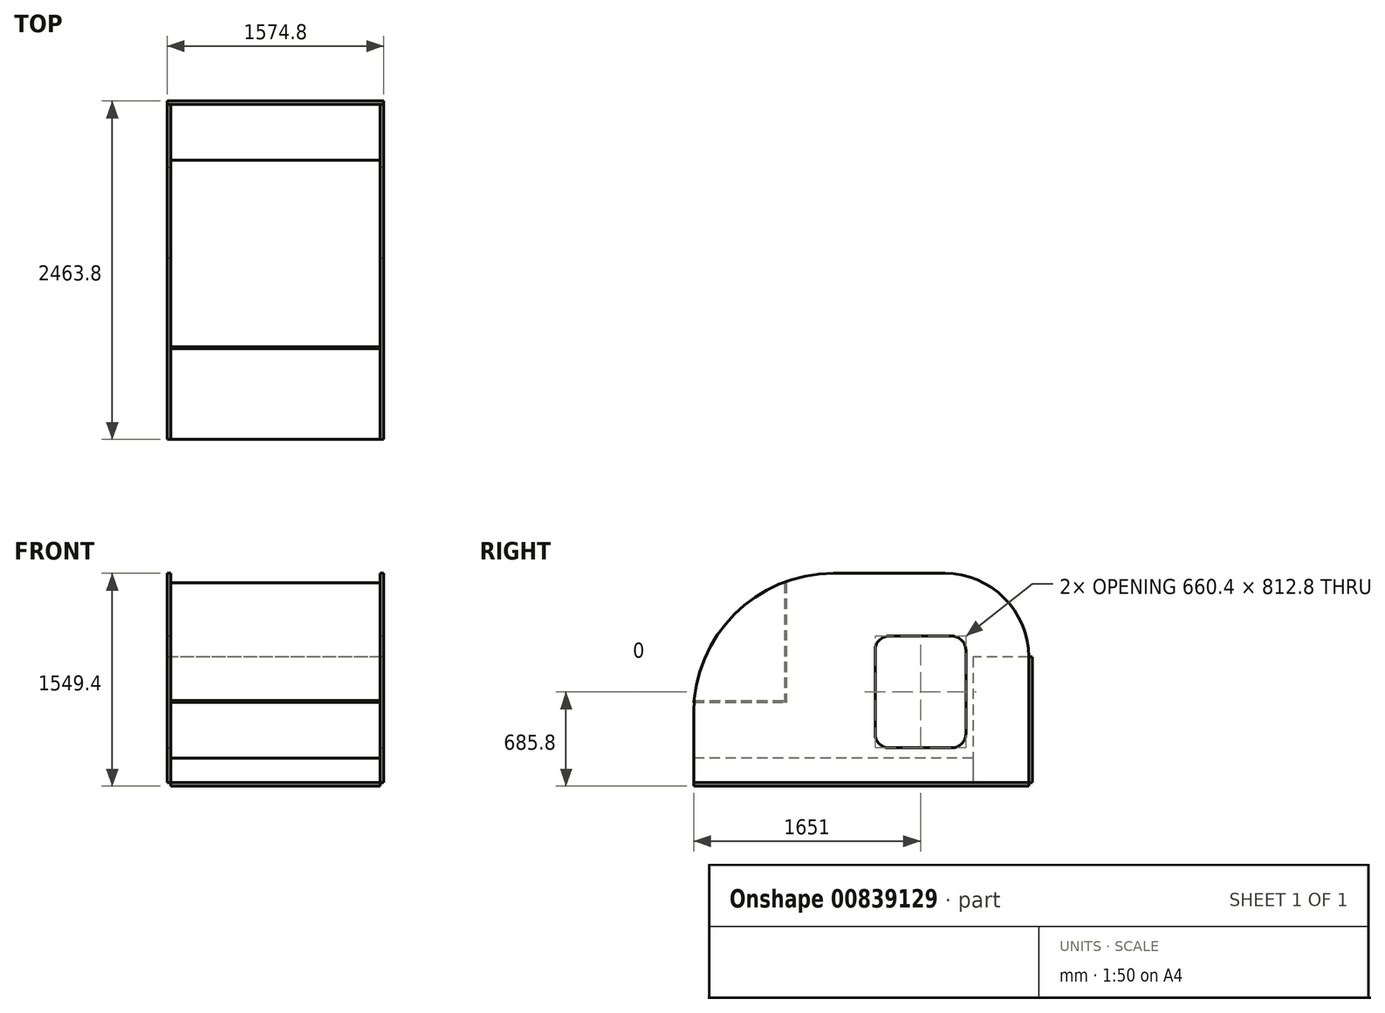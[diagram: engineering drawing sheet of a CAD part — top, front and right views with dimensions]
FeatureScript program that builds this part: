
annotation { "Feature Type Name" : "Feature", "Feature Type Description" : "" }
export const myFeature = defineFeature(function(context is Context, id is Id, definition is map)
    precondition{}
    {
        {
            var Q0;
            Q0=qCreatedBy(makeId("Right.planeOp"),FACE);
            var sketch = newSketch(context, id + "F0", { "sketchPlane" : qUnion([Q0])});
            skLineSegment(sketch, "E0.bottom", {"start": v(0, 0) * mm, "end": v(-2438.4, 0) * mm});
            skLineSegment(sketch, "E0.top", {"start": v(0, 1524) * mm, "end": v(-2438.4, 1524) * mm});
            skLineSegment(sketch, "E0.left", {"start": v(0, 0) * mm, "end": v(0, 1524) * mm});
            skLineSegment(sketch, "E0.right", {"start": v(-2438.4, 0) * mm, "end": v(-2438.4, 1524) * mm});
            skSolve(sketch);
        }
        {
            var Q0;
            Q0 = qSketchRegion(id + "F0", true);
            extrude(context, id + "F1", {"entities" : qUnion([Q0]), "depth" : 25.4 * mm, "offsetDistance" : 25.4 * mm});
        }
        {
            var Q0;
            Q0=makeQuery(id+"F1.opExtrude","CAP_FACE",FACE,{"disambiguationData":[OSD([sQuery(id+"F0.wireOp",EDGE,"E0.bottom"),sQuery(id+"F0.wireOp",EDGE,"E0.top"),sQuery(id+"F0.wireOp",EDGE,"E0.left"),sQuery(id+"F0.wireOp",EDGE,"E0.right")])],"isStart":false});
            var sketch = newSketch(context, id + "F2", { "sketchPlane" : qUnion([Q0])});
            skPoint(sketch, "E1", {"position": v(-2438.4, 508) * mm});
            skPoint(sketch, "E2", {"position": v(0, 914.4) * mm});
            skArc(sketch, "E3", {"start": v(-1422.4, 1524) * mm, "mid": v(-2140.82, 1226.42) * mm, "end": v(-2438.4, 508) * mm});
            skLineSegment(sketch, "E4", {"start": v(-1422.4, 1524) * mm, "end": v(-2438.4, 1524) * mm});
            skLineSegment(sketch, "E5", {"start": v(-2438.4, 1524) * mm, "end": v(-2438.4, 508) * mm});
            skArc(sketch, "E6", {"start": v(0, 914.4) * mm, "mid": v(-178.55, 1345.45) * mm, "end": v(-609.6, 1524) * mm});
            skLineSegment(sketch, "E7", {"start": v(-609.6, 1524) * mm, "end": v(0, 1524) * mm});
            skLineSegment(sketch, "E8", {"start": v(0, 1524) * mm, "end": v(0, 914.4) * mm});
            skSolve(sketch);
        }
        {
            var Q0;
            Q0 = qSketchRegion(id + "F2", true);
            extrude(context, id + "F3", {"entities" : qUnion([Q0]), "operationType" : NewBodyOperationType.REMOVE, "endBound" : BoundingType.THROUGH_ALL, "oppositeDirection" : true, "depth" : 25.4 * mm, "offsetDistance" : 25.4 * mm});
        }
        {
            var Q0;
            Q0=qCreatedBy(makeId("Top.planeOp"),FACE);
            var sketch = newSketch(context, id + "F4", { "sketchPlane" : qUnion([Q0])});
            skLineSegment(sketch, "E9.bottom", {"start": v(0, 0) * mm, "end": v(-1524, 0) * mm});
            skLineSegment(sketch, "E9.top", {"start": v(0, -2438.4) * mm, "end": v(-1524, -2438.4) * mm});
            skLineSegment(sketch, "E9.left", {"start": v(0, 0) * mm, "end": v(0, -2438.4) * mm});
            skLineSegment(sketch, "E9.right", {"start": v(-1524, 0) * mm, "end": v(-1524, -2438.4) * mm});
            skSolve(sketch);
        }
        {
            var Q0;
            Q0 = qSketchRegion(id + "F4", true);
            extrude(context, id + "F5", {"entities" : qUnion([Q0]), "operationType" : NewBodyOperationType.ADD, "oppositeDirection" : true, "depth" : 25.4 * mm, "offsetDistance" : 25.4 * mm});
        }
        {
            var Q0;
            Q0=qCreatedBy(makeId("Right.planeOp"),FACE);
            cPlane(context, id + "F6", {"entities" : qUnion([Q0]), "cplaneType" : CPlaneType.OFFSET, "offset" : 762 * mm, "oppositeDirection" : true, "width" : 152.4 * mm, "height" : 152.4 * mm});
        }
        {
            var Q0;
            Q0=makeQuery(id+"F1.opExtrude","SWEPT_BODY",BODY,{"disambiguationData":[OSD([sQuery(id+"F0.wireOp",EDGE,"E0.bottom"),sQuery(id+"F0.wireOp",EDGE,"E0.top"),sQuery(id+"F0.wireOp",EDGE,"E0.left"),sQuery(id+"F0.wireOp",EDGE,"E0.right")])]});
            var Q1;
            Q1=qCreatedBy(id+"F6.planeOp",FACE);
            mirror(context, id + "F7", {"operationType" : NewBodyOperationType.ADD, "entities" : qUnion([Q0]), "mirrorPlane" : qUnion([Q1])});
        }
        {
            var Q0;
            Q0=makeQuery(id+"F1.opExtrude","SWEPT_FACE",FACE,{"disambiguationData":[OSD([sQuery(id+"F0.wireOp",EDGE,"E0.left")])]});
            var sketch = newSketch(context, id + "F8", { "sketchPlane" : qUnion([Q0])});
            skLineSegment(sketch, "E10.bottom", {"start": v(-25.4, 914.4) * mm, "end": v(1549.38, 914.4) * mm});
            skLineSegment(sketch, "E10.top", {"start": v(-25.4, 0) * mm, "end": v(1549.38, 0) * mm});
            skLineSegment(sketch, "E10.left", {"start": v(-25.4, 914.4) * mm, "end": v(-25.4, 0) * mm});
            skLineSegment(sketch, "E10.right", {"start": v(1549.38, 914.4) * mm, "end": v(1549.38, 0) * mm});
            skSolve(sketch);
        }
        {
            var Q0;
            Q0 = qSketchRegion(id + "F8", true);
            extrude(context, id + "F9", {"entities" : qUnion([Q0]), "depth" : 25.4 * mm, "offsetDistance" : 25.4 * mm});
        }
        {
            var Q0;
            Q0=makeQuery(id+"F1.opExtrude","CAP_FACE",FACE,{"disambiguationData":[OSD([sQuery(id+"F0.wireOp",EDGE,"E0.bottom"),sQuery(id+"F0.wireOp",EDGE,"E0.top"),sQuery(id+"F0.wireOp",EDGE,"E0.left"),sQuery(id+"F0.wireOp",EDGE,"E0.right")])],"isStart":false});
            var sketch = newSketch(context, id + "F10", { "sketchPlane" : qUnion([Q0])});
            skLineSegment(sketch, "E11.bottom", {"start": v(-1016, 1066.8) * mm, "end": v(-558.8, 1066.8) * mm});
            skLineSegment(sketch, "E11.top", {"start": v(-1016, 254) * mm, "end": v(-558.8, 254) * mm});
            skLineSegment(sketch, "E11.left", {"start": v(-1117.6, 965.2) * mm, "end": v(-1117.6, 355.6) * mm});
            skLineSegment(sketch, "E11.right", {"start": v(-457.2, 965.2) * mm, "end": v(-457.2, 355.6) * mm});
            skPoint(sketch, "E12.visualSharp", {"position": v(-1117.6, 1066.8) * mm});
            skArc(sketch, "E12.filletArc", {"start": v(-1016, 1066.8) * mm, "mid": v(-1087.84, 1037.04) * mm, "end": v(-1117.6, 965.2) * mm});
            skPoint(sketch, "E13.visualSharp", {"position": v(-457.2, 1066.8) * mm});
            skArc(sketch, "E13.filletArc", {"start": v(-457.2, 965.2) * mm, "mid": v(-486.96, 1037.04) * mm, "end": v(-558.8, 1066.8) * mm});
            skPoint(sketch, "E14.visualSharp", {"position": v(-1117.6, 254) * mm});
            skArc(sketch, "E14.filletArc", {"start": v(-1117.6, 355.6) * mm, "mid": v(-1087.84, 283.76) * mm, "end": v(-1016, 254) * mm});
            skPoint(sketch, "E15.visualSharp", {"position": v(-457.2, 254) * mm});
            skArc(sketch, "E15.filletArc", {"start": v(-558.8, 254) * mm, "mid": v(-486.96, 283.76) * mm, "end": v(-457.2, 355.6) * mm});
            skSolve(sketch);
        }
        {
            var Q0;
            Q0 = qSketchRegion(id + "F10", true);
            var Q1;
            Q1=makeQuery(id+"F7.opPattern","COPY",FACE,{"derivedFrom":makeQuery(id+"F1.opExtrude","CAP_FACE",FACE,{"disambiguationData":[OSD([sQuery(id+"F0.wireOp",EDGE,"E0.bottom"),sQuery(id+"F0.wireOp",EDGE,"E0.top"),sQuery(id+"F0.wireOp",EDGE,"E0.left"),sQuery(id+"F0.wireOp",EDGE,"E0.right")])],"isStart":false}),"instanceName":"1"});
            extrude(context, id + "F11", {"entities" : qUnion([Q0]), "operationType" : NewBodyOperationType.REMOVE, "oppositeDirection" : true, "depth" : 1574.8 * mm, "endBoundEntityFace" : qUnion([Q1]), "offsetDistance" : 25.4 * mm});
        }
        {
            var Q0;
            Q0=makeQuery(id+"F5.opExtrude","CAP_FACE",FACE,{"disambiguationData":[OSD([sQuery(id+"F4.wireOp",EDGE,"E9.bottom"),sQuery(id+"F4.wireOp",EDGE,"E9.top"),sQuery(id+"F4.wireOp",EDGE,"E9.left"),sQuery(id+"F4.wireOp",EDGE,"E9.right")])],"isStart":true});
            var sketch = newSketch(context, id + "F12", { "sketchPlane" : qUnion([Q0])});
            skLineSegment(sketch, "E16.bottom", {"start": v(-1524, -2438.4) * mm, "end": v(0, -2438.4) * mm});
            skLineSegment(sketch, "E16.top", {"start": v(-1524, -406.4) * mm, "end": v(0, -406.4) * mm});
            skLineSegment(sketch, "E16.left", {"start": v(-1524, -2438.4) * mm, "end": v(-1524, -406.4) * mm});
            skLineSegment(sketch, "E16.right", {"start": v(0, -2438.4) * mm, "end": v(0, -406.4) * mm});
            skSolve(sketch);
        }
        {
            var Q0;
            Q0 = qSketchRegion(id + "F12", true);
            extrude(context, id + "F13", {"entities" : qUnion([Q0]), "depth" : 177.8 * mm, "offsetDistance" : 25.4 * mm});
        }
        {
            var Q0;
            Q0=makeQuery(id+"F13.opExtrude","CAP_FACE",FACE,{"disambiguationData":[OSD([sQuery(id+"F12.wireOp",EDGE,"E16.bottom"),sQuery(id+"F12.wireOp",EDGE,"E16.top"),sQuery(id+"F12.wireOp",EDGE,"E16.left"),sQuery(id+"F12.wireOp",EDGE,"E16.right")])],"isStart":false});
            cPlane(context, id + "F14", {"entities" : qUnion([Q0]), "cplaneType" : CPlaneType.OFFSET, "offset" : 406.4 * mm, "width" : 152.4 * mm, "height" : 152.4 * mm});
        }
        {
            var Q0;
            Q0=qCreatedBy(id+"F14.planeOp",FACE);
            var sketch = newSketch(context, id + "F15", { "sketchPlane" : qUnion([Q0])});
            skLineSegment(sketch, "E17.bottom", {"start": v(-1524, -2438.4) * mm, "end": v(0, -2438.4) * mm});
            skLineSegment(sketch, "E17.top", {"start": v(-1524, -1778) * mm, "end": v(0, -1778) * mm});
            skLineSegment(sketch, "E17.left", {"start": v(-1524, -2438.4) * mm, "end": v(-1524, -1778) * mm});
            skLineSegment(sketch, "E17.right", {"start": v(0, -2438.4) * mm, "end": v(0, -1778) * mm});
            skSolve(sketch);
        }
        {
            var Q0;
            Q0 = qSketchRegion(id + "F15", true);
            extrude(context, id + "F16", {"entities" : qUnion([Q0]), "depth" : 12.7 * mm, "offsetDistance" : 25.4 * mm});
        }
        {
            var Q0;
            Q0=makeQuery(id+"F16.opExtrude","SWEPT_FACE",FACE,{"disambiguationData":[OSD([sQuery(id+"F15.wireOp",EDGE,"E17.top")])]});
            var sketch = newSketch(context, id + "F17", { "sketchPlane" : qUnion([Q0])});
            skLineSegment(sketch, "E18.bottom", {"start": v(0, 584.2) * mm, "end": v(1524, 584.2) * mm});
            skLineSegment(sketch, "E18.top", {"start": v(0, 1455.2) * mm, "end": v(1524, 1455.2) * mm});
            skLineSegment(sketch, "E18.left", {"start": v(0, 584.2) * mm, "end": v(0, 1455.2) * mm});
            skLineSegment(sketch, "E18.right", {"start": v(1524, 584.2) * mm, "end": v(1524, 1455.2) * mm});
            skSolve(sketch);
        }
        {
            var Q0;
            Q0 = qSketchRegion(id + "F17", true);
            extrude(context, id + "F18", {"entities" : qUnion([Q0]), "depth" : 12.7 * mm, "offsetDistance" : 25.4 * mm});
        }
        {
            var Q0;
            Q0=makeQuery(id+"F5.opExtrude","CAP_FACE",FACE,{"disambiguationData":[OSD([sQuery(id+"F4.wireOp",EDGE,"E9.bottom"),sQuery(id+"F4.wireOp",EDGE,"E9.top"),sQuery(id+"F4.wireOp",EDGE,"E9.left"),sQuery(id+"F4.wireOp",EDGE,"E9.right")])],"isStart":true});
            var sketch = newSketch(context, id + "F19", { "sketchPlane" : qUnion([Q0])});
            skLineSegment(sketch, "E19.bottom", {"start": v(0, 0) * mm, "end": v(-1524, 0) * mm});
            skLineSegment(sketch, "E19.top", {"start": v(0, -403.9) * mm, "end": v(-1524, -403.9) * mm});
            skLineSegment(sketch, "E19.left", {"start": v(0, 0) * mm, "end": v(0, -403.9) * mm});
            skLineSegment(sketch, "E19.right", {"start": v(-1524, 0) * mm, "end": v(-1524, -403.9) * mm});
            skSolve(sketch);
        }
        {
            var Q0;
            Q0 = qSketchRegion(id + "F19", true);
            extrude(context, id + "F20", {"entities" : qUnion([Q0]), "depth" : 914.4 * mm, "offsetDistance" : 25.4 * mm});
        }
    });
